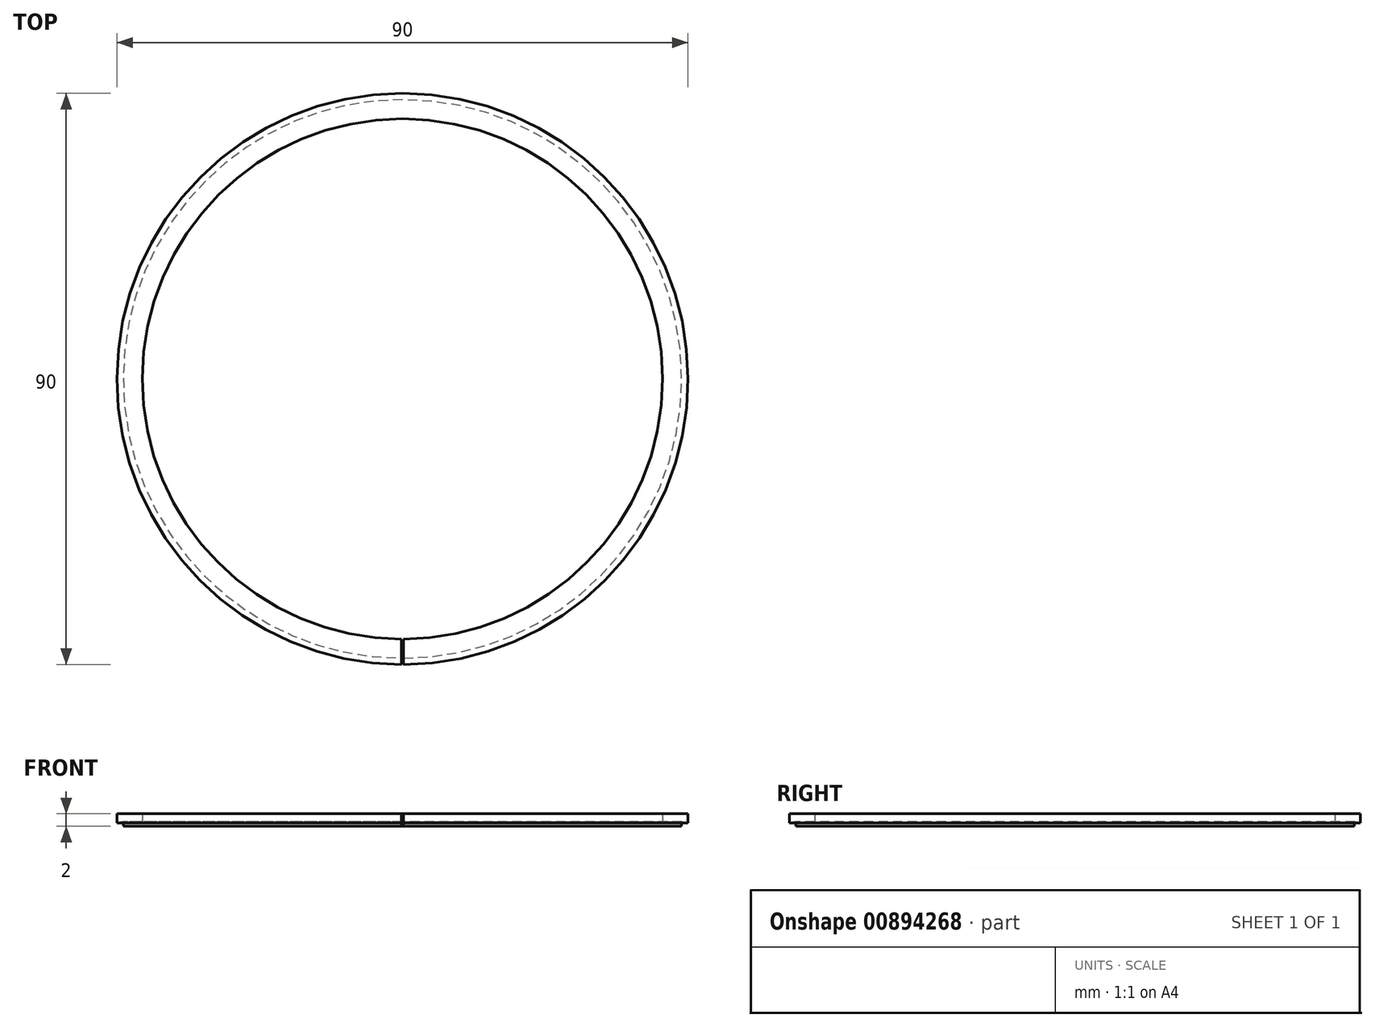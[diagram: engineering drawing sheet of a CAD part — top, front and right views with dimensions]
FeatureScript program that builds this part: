
annotation { "Feature Type Name" : "Feature", "Feature Type Description" : "" }
export const myFeature = defineFeature(function(context is Context, id is Id, definition is map)
    precondition{}
    {
        {
            var Q0;
            Q0=qCreatedBy(makeId("Right.planeOp"),FACE);
            var sketch = newSketch(context, id + "F0", { "sketchPlane" : qUnion([Q0])});
            skLineSegment(sketch, "E0", {"start": v(0, 0) * mm, "end": v(41, 0) * mm, "construction": true});
            skLineSegment(sketch, "E1.bottom", {"start": v(41, 2) * mm, "end": v(45, 2) * mm});
            skLineSegment(sketch, "E1.left", {"start": v(41, 2) * mm, "end": v(41, 0) * mm});
            skLineSegment(sketch, "E1.right", {"start": v(45, 2) * mm, "end": v(45, 0.5) * mm});
            skLineSegment(sketch, "E2", {"start": v(44, 0.6) * mm, "end": v(44, 0) * mm});
            skLineSegment(sketch, "E3", {"start": v(44.12, 0.7) * mm, "end": v(45, 0.5) * mm});
            skPoint(sketch, "E4.visualSharp", {"position": v(44, 0.73) * mm});
            skArc(sketch, "E4.filletArc", {"start": v(44.12, 0.7) * mm, "mid": v(44.04, 0.68) * mm, "end": v(44, 0.6) * mm});
            skLineSegment(sketch, "E5", {"start": v(41, 0) * mm, "end": v(44, 0) * mm});
            skLineSegment(sketch, "E6", {"start": v(0, 0) * mm, "end": v(0, 20) * mm, "construction": true});
            skSolve(sketch);
        }
        {
            var Q0;
            Q0=makeQuery(id+"F0.imprint","IMPRINT",FACE,{"disambiguationData":[TD([[makeQuery(id+"F0.imprint","IMPRINT",EDGE,{"derivedFrom":sQuery(id+"F0.wireOp",EDGE,"E1.bottom")}),-1.0]])]});
            var Q1;
            Q1=sQuery(id+"F0.wireOp",EDGE,"E6");
            revolve(context, id + "F1", {"surfaceOperationType" : NewSurfaceOperationType.NEW, "entities" : qUnion([Q0]), "axis" : qUnion([Q1]), "revolveType" : RevolveType.TWO_DIRECTIONS, "angle" : 179.8 * degree, "angleBack" : 180.2 * degree});
        }
    });
